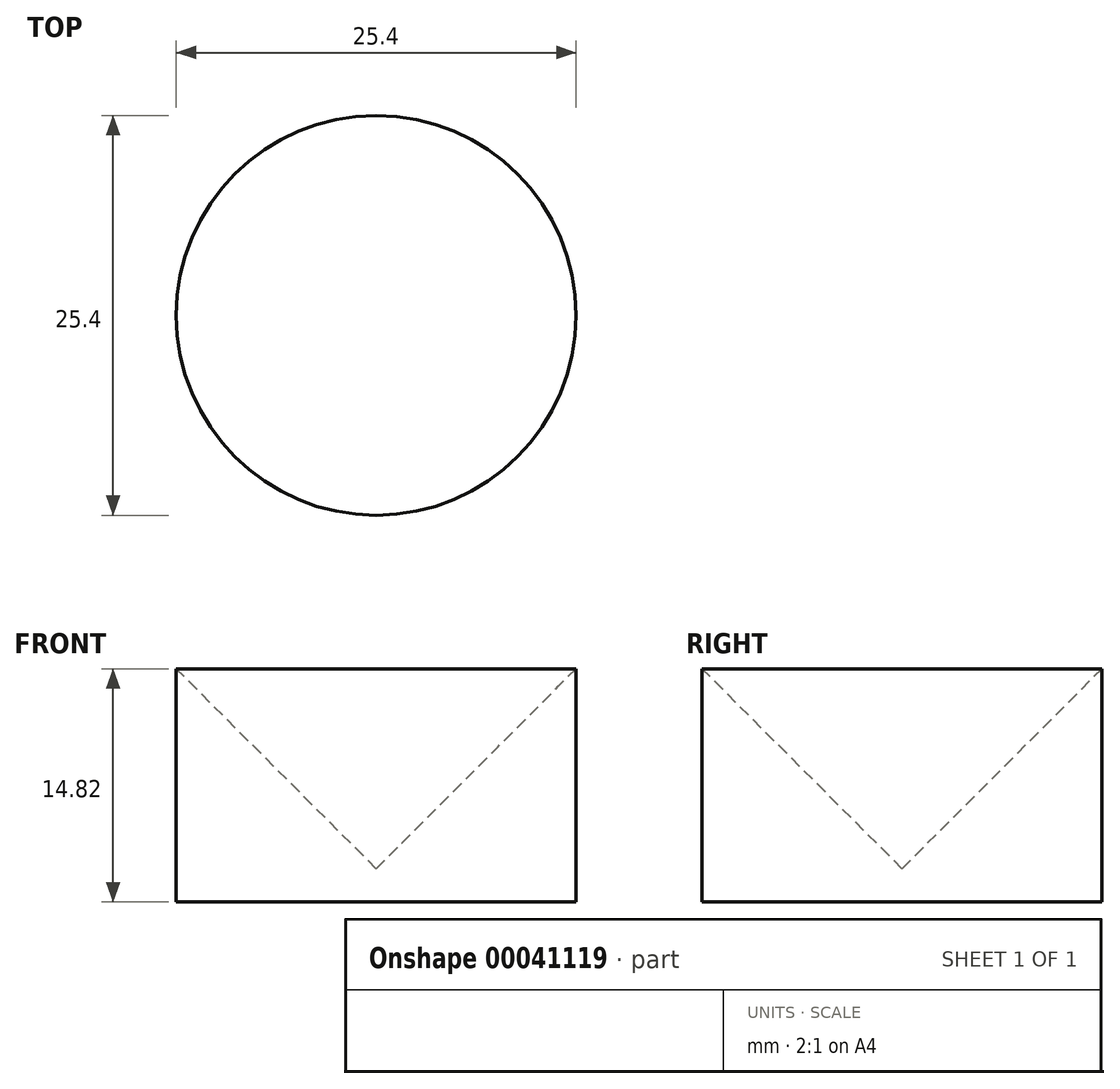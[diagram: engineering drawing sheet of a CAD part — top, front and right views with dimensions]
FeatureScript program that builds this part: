
annotation { "Feature Type Name" : "Feature", "Feature Type Description" : "" }
export const myFeature = defineFeature(function(context is Context, id is Id, definition is map)
    precondition{}
    {
        {
            var Q0;
            Q0=qCreatedBy(makeId("Front.planeOp"),FACE);
            var sketch = newSketch(context, id + "F0", { "sketchPlane" : qUnion([Q0])});
            skLineSegment(sketch, "E0", {"start": v(0, 0) * mm, "end": v(0, 18.63) * mm, "construction": true});
            skSolve(sketch);
        }
        {
            var Q0;
            Q0=qCreatedBy(makeId("Front.planeOp"),FACE);
            var sketch = newSketch(context, id + "F1", { "sketchPlane" : qUnion([Q0])});
            skLineSegment(sketch, "E1", {"start": v(0, 0) * mm, "end": v(12.7, 12.7) * mm});
            skLineSegment(sketch, "E2", {"start": v(12.7, 12.7) * mm, "end": v(12.7, -2.12) * mm});
            skLineSegment(sketch, "E3", {"start": v(12.7, -2.12) * mm, "end": v(0, -2.12) * mm});
            skLineSegment(sketch, "E4", {"start": v(0, -2.12) * mm, "end": v(0, 0) * mm});
            skSolve(sketch);
        }
        {
            var Q0;
            Q0=makeQuery(id+"F1.imprint","IMPRINT",FACE,{"disambiguationData":[TD([[makeQuery(id+"F1.imprint","IMPRINT",EDGE,{"derivedFrom":sQuery(id+"F1.wireOp",EDGE,"E1")}),-1.0]])]});
            var Q1;
            Q1=sQuery(id+"F0.wireOp",EDGE,"E0");
            revolve(context, id + "F2", {"entities" : qUnion([Q0]), "axis" : qUnion([Q1]), "revolveType" : RevolveType.FULL});
        }
    });
